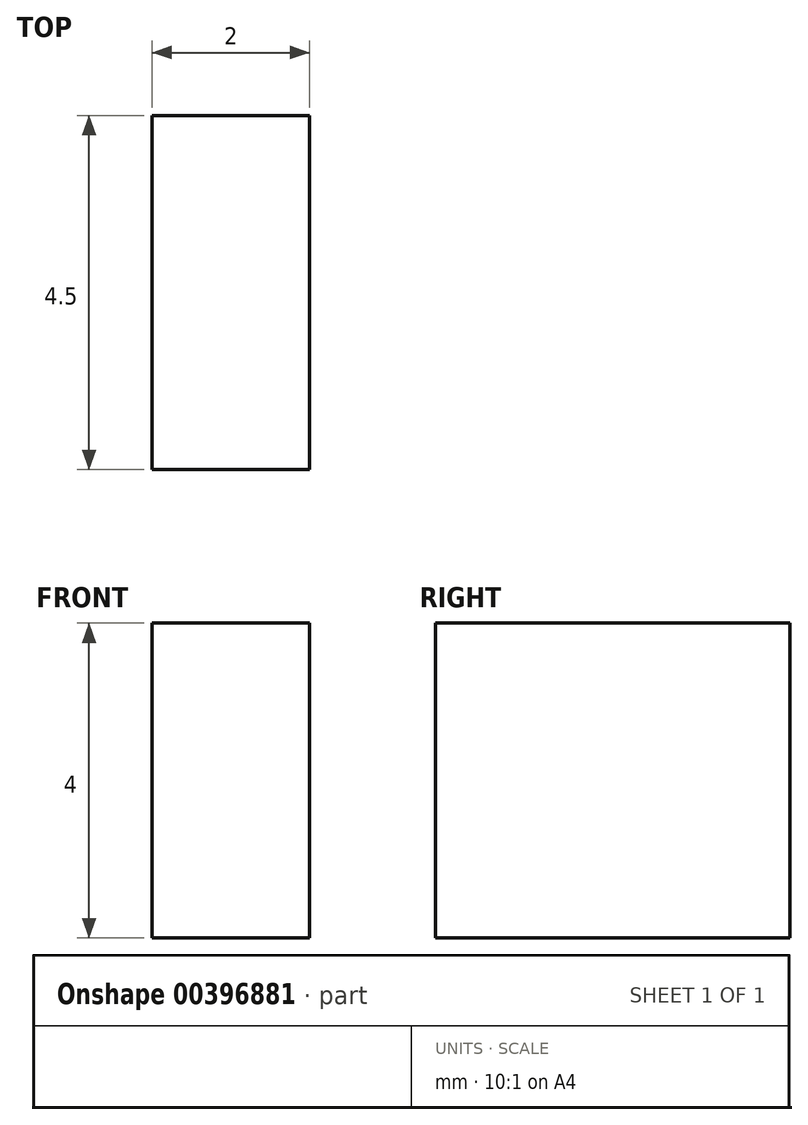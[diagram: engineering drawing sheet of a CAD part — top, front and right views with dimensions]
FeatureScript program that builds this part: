
annotation { "Feature Type Name" : "Feature", "Feature Type Description" : "" }
export const myFeature = defineFeature(function(context is Context, id is Id, definition is map)
    precondition{}
    {
        {
            var Q0;
            Q0=qCreatedBy(makeId("Top.planeOp"),FACE);
            var sketch = newSketch(context, id + "F0", { "sketchPlane" : qUnion([Q0])});
            skLineSegment(sketch, "E0.bottom", {"start": v(1.08, -14.7) * mm, "end": v(-0.92, -14.7) * mm});
            skLineSegment(sketch, "E0.top", {"start": v(1.08, -19.2) * mm, "end": v(-0.92, -19.2) * mm});
            skLineSegment(sketch, "E0.left", {"start": v(1.08, -14.7) * mm, "end": v(1.08, -19.2) * mm});
            skLineSegment(sketch, "E0.right", {"start": v(-0.92, -14.7) * mm, "end": v(-0.92, -19.2) * mm});
            skSolve(sketch);
        }
        {
            var Q0;
            Q0=makeQuery(id+"F0.imprint","IMPRINT",FACE,{"disambiguationData":[TD([[makeQuery(id+"F0.imprint","IMPRINT",EDGE,{"derivedFrom":sQuery(id+"F0.wireOp",EDGE,"tyr0sLR0-9LCc-QaAx-F8TZ-KkOKVTJG4uO9.bottom")}),-1.0]])]});
            var Q1;
            Q1=makeQuery(id+"F0.imprint","IMPRINT",FACE,{"disambiguationData":[TD([[makeQuery(id+"F0.imprint","IMPRINT",EDGE,{"derivedFrom":sQuery(id+"F0.wireOp",EDGE,"myyxiUY7-CIvu-58U3-XXL2-zQbjcas5zoq9.bottom")}),1.0]])]});
            var Q2;
            Q2=makeQuery(id+"F0.imprint","IMPRINT",FACE,{"disambiguationData":[TD([[makeQuery(id+"F0.imprint","IMPRINT",EDGE,{"derivedFrom":sQuery(id+"F0.wireOp",EDGE,"E0.bottom")}),1.0]])]});
            extrude(context, id + "F1", {"entities" : qUnion([Q0, Q1, Q2]), "depth" : 4 * mm});
        }
    });
